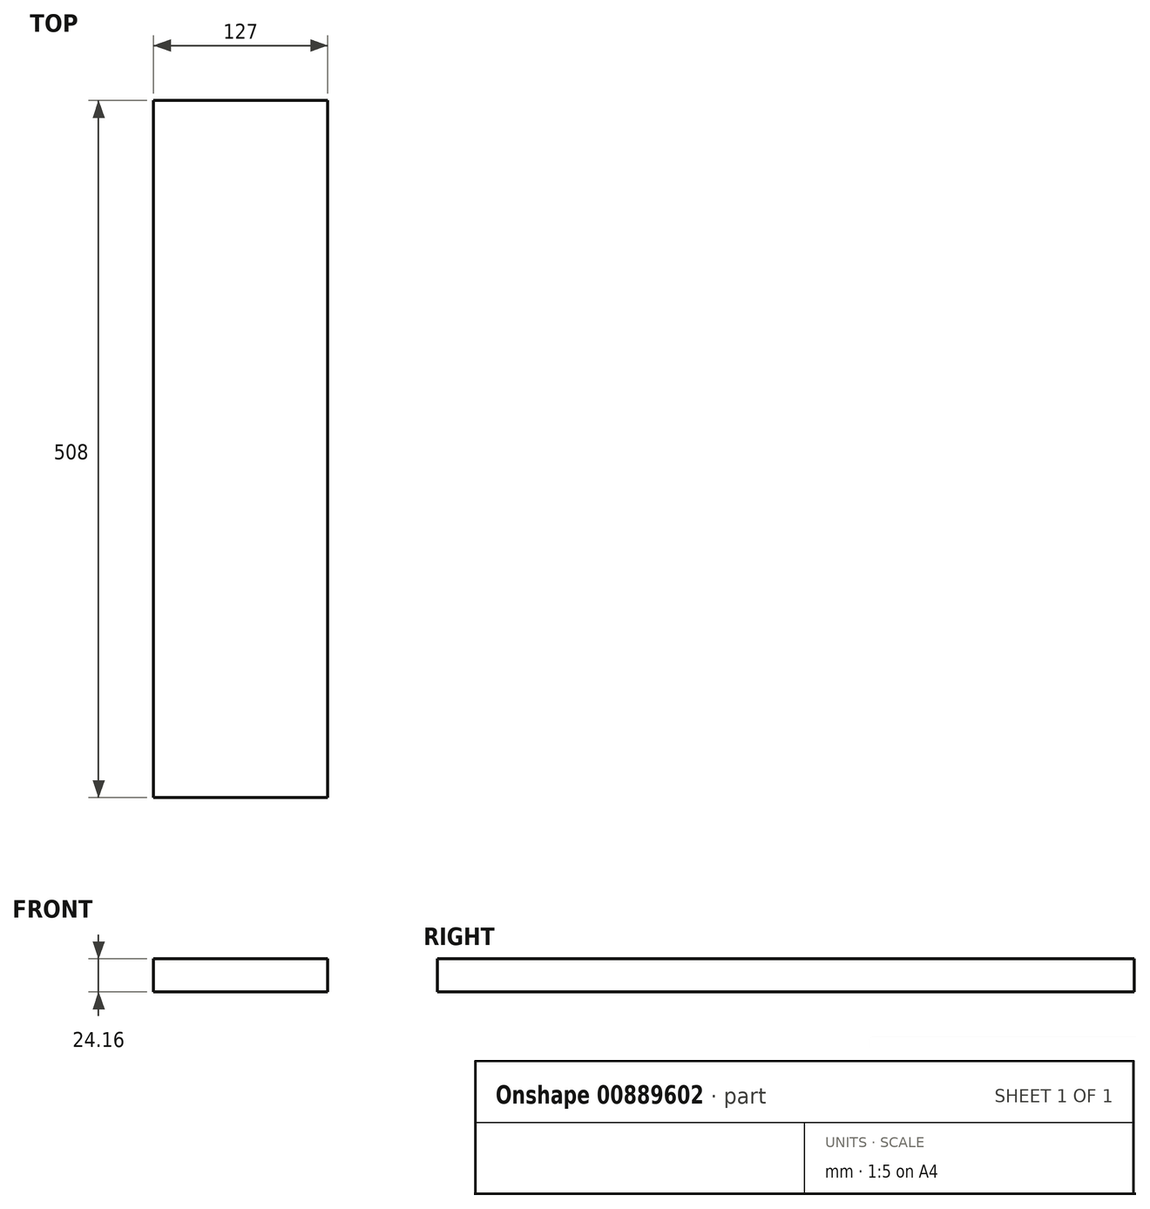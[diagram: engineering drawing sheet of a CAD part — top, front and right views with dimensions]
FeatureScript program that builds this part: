
annotation { "Feature Type Name" : "Feature", "Feature Type Description" : "" }
export const myFeature = defineFeature(function(context is Context, id is Id, definition is map)
    precondition{}
    {
        {
            var Q0;
            Q0=qCreatedBy(makeId("Front.planeOp"),FACE);
            var sketch = newSketch(context, id + "F0", { "sketchPlane" : qUnion([Q0])});
            skLineSegment(sketch, "E0.bottom", {"start": v(-63.5, 12.08) * mm, "end": v(63.5, 12.08) * mm});
            skLineSegment(sketch, "E0.top", {"start": v(-63.5, -12.08) * mm, "end": v(63.5, -12.08) * mm});
            skLineSegment(sketch, "E0.left", {"start": v(-63.5, 12.08) * mm, "end": v(-63.5, -12.08) * mm});
            skLineSegment(sketch, "E0.right", {"start": v(63.5, 12.08) * mm, "end": v(63.5, -12.08) * mm});
            skPoint(sketch, "E0.middle", {"position": v(0, 0) * mm});
            skLineSegment(sketch, "E1", {"start": v(-63.5, 12.08) * mm, "end": v(-63.5, 68.85) * mm});
            skLineSegment(sketch, "E2", {"start": v(63.5, 12.08) * mm, "end": v(63.5, 68.85) * mm});
            skLineSegment(sketch, "E3", {"start": v(-63.5, 68.85) * mm, "end": v(63.5, 68.85) * mm});
            skSolve(sketch);
        }
        {
            var Q0;
            Q0=makeQuery(id+"F0.imprint","IMPRINT",FACE,{"disambiguationData":[TD([[makeQuery(id+"F0.imprint","IMPRINT",EDGE,{"derivedFrom":sQuery(id+"F0.wireOp",EDGE,"E0.bottom")}),-1.0]])]});
            extrude(context, id + "F1", {"entities" : qUnion([Q0]), "depth" : 508 * mm, "offsetDistance" : 25.4 * mm});
        }
    });
